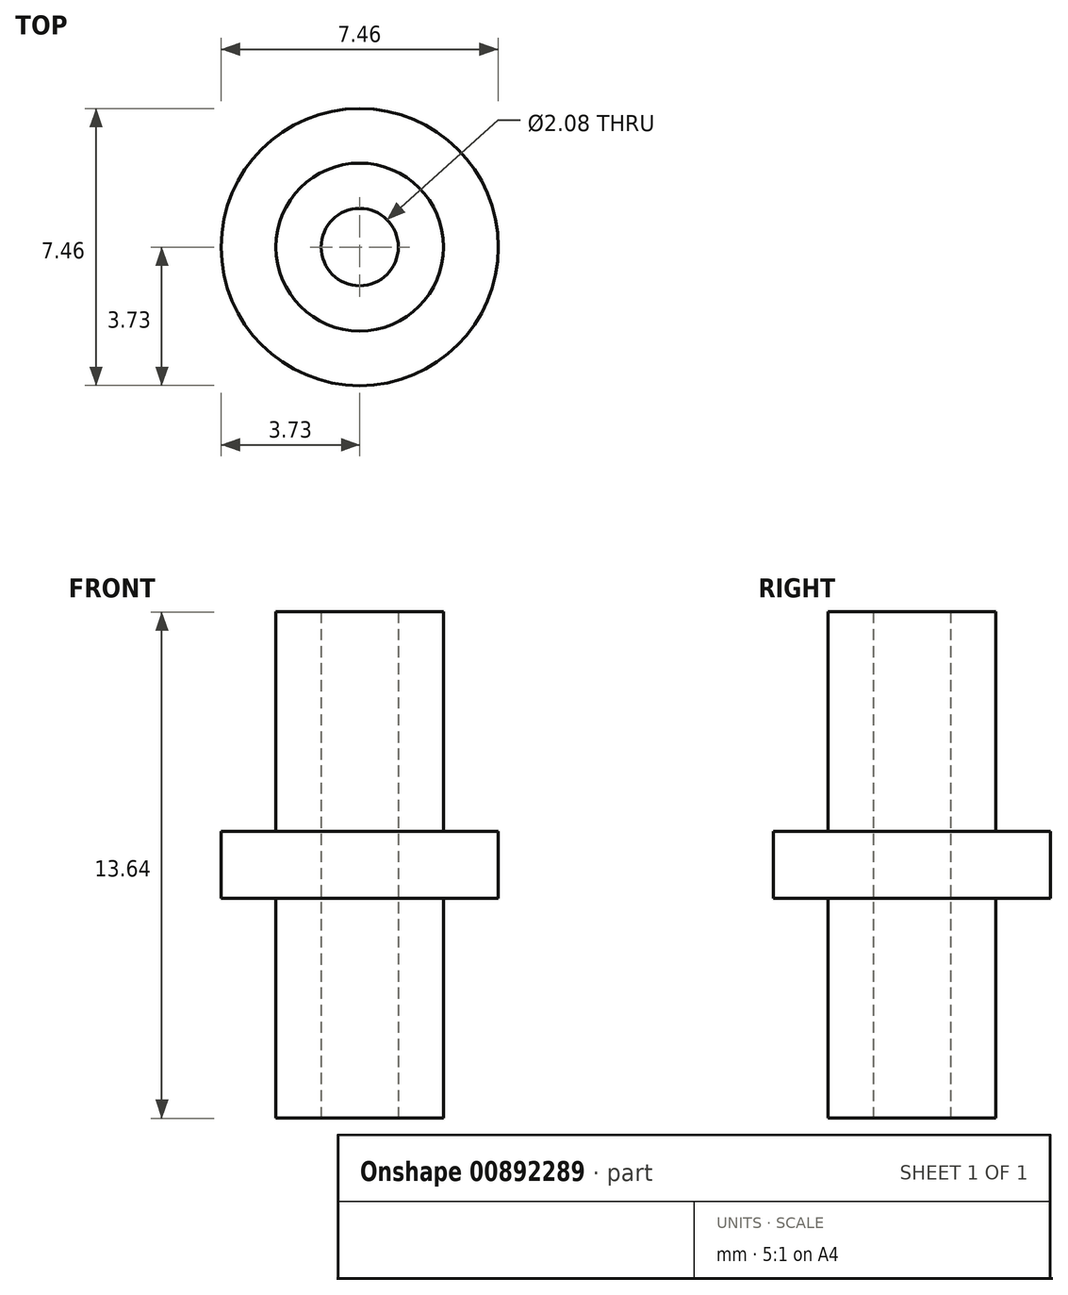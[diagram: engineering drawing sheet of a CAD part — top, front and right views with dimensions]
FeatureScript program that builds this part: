
annotation { "Feature Type Name" : "Feature", "Feature Type Description" : "" }
export const myFeature = defineFeature(function(context is Context, id is Id, definition is map)
    precondition{}
    {
        {
            var Q0;
            Q0=qCreatedBy(makeId("Top.planeOp"),FACE);
            var sketch = newSketch(context, id + "F0", { "sketchPlane" : qUnion([Q0])});
            skCircle(sketch, "E0", {"center": v(0, 0) * mm, "radius": 3.73 * mm});
            skSolve(sketch);
        }
        {
            var Q0;
            Q0=qSketchRegion(id+"F0",true);
            extrude(context, id + "F1", {"entities" : qUnion([Q0]), "depth" : 1.8 * mm, "offsetDistance" : 25.4 * mm});
        }
        {
            var Q0;
            Q0=makeQuery(id+"F1.opExtrude","CAP_FACE",FACE,{"disambiguationData":[OSD([sQuery(id+"F0.wireOp",EDGE,"E0")])],"isStart":true});
            var sketch = newSketch(context, id + "F2", { "sketchPlane" : qUnion([Q0])});
            skCircle(sketch, "E1", {"center": v(0, 0) * mm, "radius": 2.26 * mm});
            skSolve(sketch);
        }
        {
            var Q0;
            Q0=makeQuery(id+"F2.imprint","IMPRINT",FACE,{"disambiguationData":[TD([[makeQuery(id+"F2.imprint","IMPRINT",EDGE,{"derivedFrom":sQuery(id+"F2.wireOp",EDGE,"E1")}),1.0]])]});
            extrude(context, id + "F3", {"entities" : qUnion([Q0]), "operationType" : NewBodyOperationType.ADD, "depth" : 5.92 * mm, "offsetDistance" : 25.4 * mm});
        }
        {
            var Q0;
            Q0=makeQuery(id+"F1.opExtrude","CAP_FACE",FACE,{"disambiguationData":[OSD([sQuery(id+"F0.wireOp",EDGE,"E0")])],"isStart":false});
            var sketch = newSketch(context, id + "F4", { "sketchPlane" : qUnion([Q0])});
            skCircle(sketch, "E2.0", {"center": v(0, 0) * mm, "radius": 2.26 * mm});
            skSolve(sketch);
        }
        {
            var Q0;
            Q0=qSketchRegion(id+"F4",true);
            extrude(context, id + "F5", {"entities" : qUnion([Q0]), "operationType" : NewBodyOperationType.ADD, "depth" : 5.92 * mm, "offsetDistance" : 25.4 * mm});
        }
        {
            var Q0;
            Q0=makeQuery(id+"F3.opExtrude","CAP_FACE",FACE,{"disambiguationData":[OSD([sQuery(id+"F2.wireOp",EDGE,"E1")])],"isStart":false});
            var sketch = newSketch(context, id + "F6", { "sketchPlane" : qUnion([Q0])});
            skCircle(sketch, "E3", {"center": v(0, 0) * mm, "radius": 1.04 * mm});
            skSolve(sketch);
        }
        {
            var Q0;
            Q0=makeQuery(id+"F6.imprint","IMPRINT",FACE,{"disambiguationData":[TD([[makeQuery(id+"F6.imprint","IMPRINT",EDGE,{"derivedFrom":sQuery(id+"F6.wireOp",EDGE,"E3")}),1.0]])]});
            extrude(context, id + "F7", {"entities" : qUnion([Q0]), "operationType" : NewBodyOperationType.REMOVE, "oppositeDirection" : true, "depth" : 25.4 * mm, "offsetDistance" : 25.4 * mm});
        }
    });
